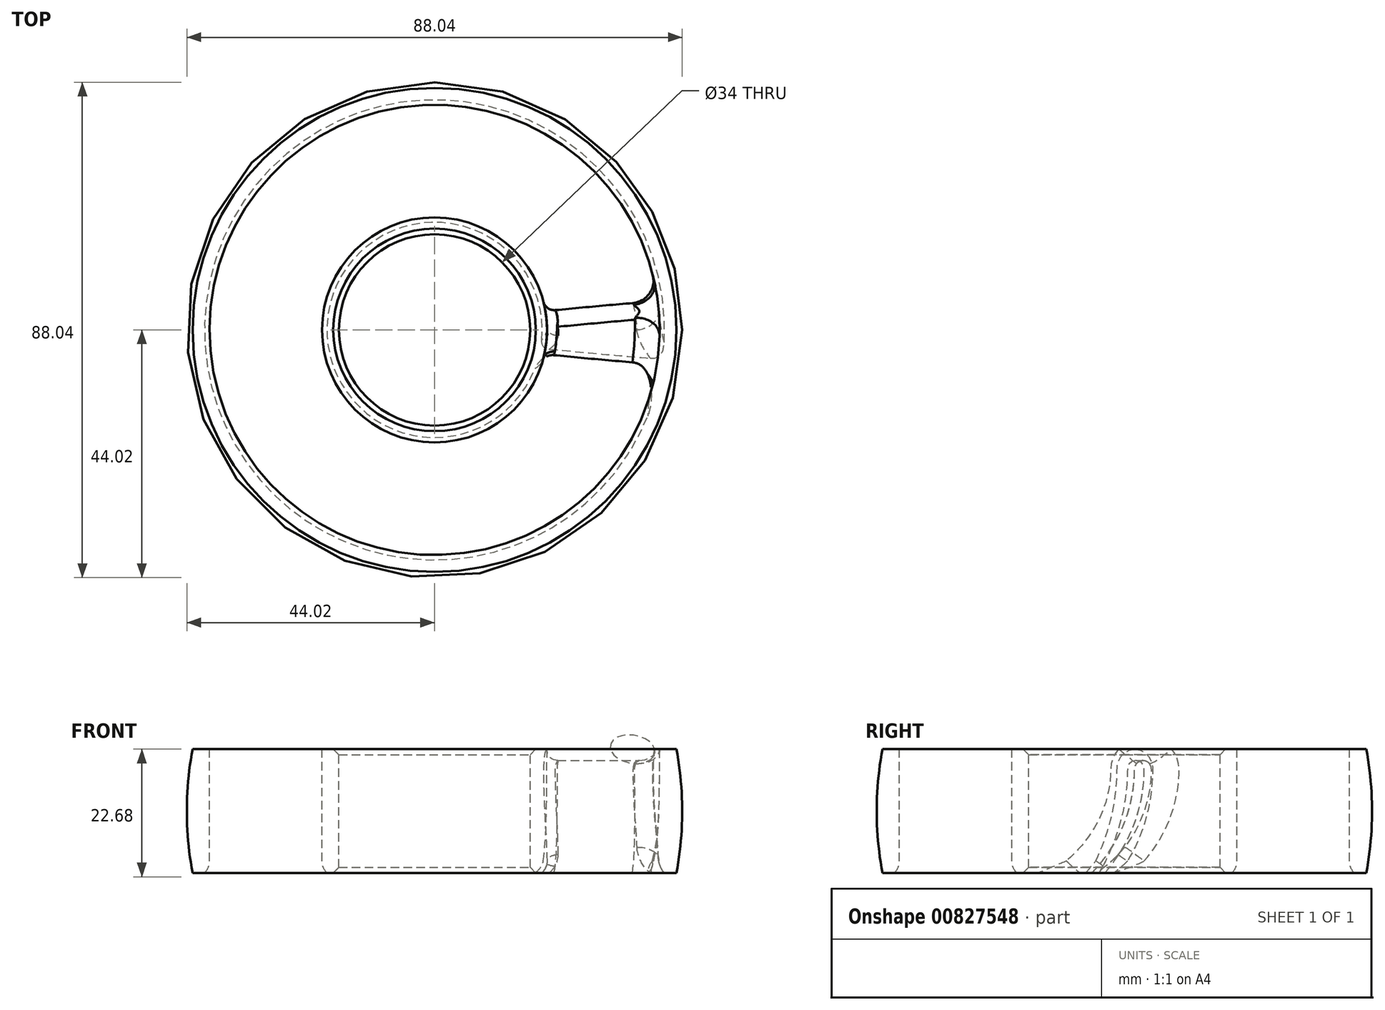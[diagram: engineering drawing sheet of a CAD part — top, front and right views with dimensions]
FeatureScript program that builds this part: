
annotation { "Feature Type Name" : "Feature", "Feature Type Description" : "" }
export const myFeature = defineFeature(function(context is Context, id is Id, definition is map)
    precondition{}
    {
        {
            var Q0;
            Q0=qCreatedBy(makeId("Right.planeOp"),FACE);
            cPlane(context, id + "F0", {"entities" : qUnion([Q0]), "cplaneType" : CPlaneType.OFFSET, "offset" : 18 * mm, "width" : 150 * mm, "height" : 150 * mm});
        }
        {
            var Q0;
            Q0=qCreatedBy(makeId("Right.planeOp"),FACE);
            cPlane(context, id + "F1", {"entities" : qUnion([Q0]), "cplaneType" : CPlaneType.OFFSET, "offset" : 30 * mm, "width" : 150 * mm, "height" : 150 * mm});
        }
        {
            var Q0;
            Q0=qCreatedBy(makeId("Right.planeOp"),FACE);
            cPlane(context, id + "F2", {"entities" : qUnion([Q0]), "cplaneType" : CPlaneType.OFFSET, "offset" : 42 * mm, "width" : 150 * mm, "height" : 150 * mm});
        }
        {
            var Q0;
            Q0=qCreatedBy(makeId("Right.planeOp"),FACE);
            var sketch = newSketch(context, id + "F3", { "sketchPlane" : qUnion([Q0])});
            skLineSegment(sketch, "E0.bottom", {"start": v(20, 10) * mm, "end": v(-20, 10) * mm});
            skLineSegment(sketch, "E0.top", {"start": v(20, -10) * mm, "end": v(-20, -10) * mm});
            skLineSegment(sketch, "E0.left", {"start": v(20, 10) * mm, "end": v(20, -10) * mm});
            skLineSegment(sketch, "E0.right", {"start": v(-20, 10) * mm, "end": v(-20, -10) * mm});
            skPoint(sketch, "E0.middle", {"position": v(0, 0) * mm});
            skSolve(sketch);
        }
        {
            var Q0;
            Q0=qCreatedBy(id+"F0.planeOp",FACE);
            var sketch = newSketch(context, id + "F4", { "sketchPlane" : qUnion([Q0])});
            skArc(sketch, "E1", {"start": v(3.19, 8.5) * mm, "mid": v(1.69, 10) * mm, "end": v(0.19, 8.5) * mm});
            skArc(sketch, "E2", {"start": v(-3.19, -10) * mm, "mid": v(1.55, -1.28) * mm, "end": v(3.19, 8.5) * mm});
            skArc(sketch, "E3", {"start": v(-4.19, -10) * mm, "mid": v(-0.92, -1) * mm, "end": v(0.19, 8.5) * mm});
            skLineSegment(sketch, "E4", {"start": v(0.19, 8.5) * mm, "end": v(3.19, 8.5) * mm, "construction": true});
            skLineSegment(sketch, "E5", {"start": v(-3.19, -10) * mm, "end": v(-4.19, -10) * mm});
            skLineSegment(sketch, "E6", {"start": v(-26.86, 8.5) * mm, "end": v(-3.19, -10) * mm, "construction": true});
            skLineSegment(sketch, "E7", {"start": v(3.19, 8.5) * mm, "end": v(3.19, -10) * mm, "construction": true});
            skLineSegment(sketch, "E8", {"start": v(-3.19, -10) * mm, "end": v(3.19, -10) * mm, "construction": true});
            skLineSegment(sketch, "E9", {"start": v(0, 0) * mm, "end": v(0, -10) * mm, "construction": true});
            skSolve(sketch);
        }
        {
            var Q0;
            Q0=qCreatedBy(id+"F1.planeOp",FACE);
            var sketch = newSketch(context, id + "F5", { "sketchPlane" : qUnion([Q0])});
            skArc(sketch, "E10", {"start": v(4.31, 8.5) * mm, "mid": v(2.81, 10) * mm, "end": v(1.31, 8.5) * mm});
            skLineSegment(sketch, "E11", {"start": v(1.31, 8.5) * mm, "end": v(4.31, 8.5) * mm, "construction": true});
            skLineSegment(sketch, "E12", {"start": v(-5.31, -10) * mm, "end": v(-4.31, -10) * mm});
            skArc(sketch, "E13", {"start": v(-4.31, -10) * mm, "mid": v(2.05, -1.7) * mm, "end": v(4.31, 8.5) * mm});
            skArc(sketch, "E14", {"start": v(-5.31, -10) * mm, "mid": v(-0.4, -1.33) * mm, "end": v(1.31, 8.5) * mm});
            skLineSegment(sketch, "E15", {"start": v(-19.84, 8.5) * mm, "end": v(-4.31, -10) * mm, "construction": true});
            skLineSegment(sketch, "E16", {"start": v(4.31, 8.5) * mm, "end": v(4.31, -10) * mm, "construction": true});
            skLineSegment(sketch, "E17", {"start": v(-4.31, -10) * mm, "end": v(4.31, -10) * mm, "construction": true});
            skLineSegment(sketch, "E18", {"start": v(0, 0) * mm, "end": v(0, -10) * mm, "construction": true});
            skSolve(sketch);
        }
        {
            var Q0;
            Q0=qCreatedBy(id+"F2.planeOp",FACE);
            var sketch = newSketch(context, id + "F6", { "sketchPlane" : qUnion([Q0])});
            skArc(sketch, "E19", {"start": v(5.34, 8.5) * mm, "mid": v(3.84, 10) * mm, "end": v(2.34, 8.5) * mm});
            skLineSegment(sketch, "E20", {"start": v(-6.34, -10) * mm, "end": v(-5.34, -10) * mm});
            skLineSegment(sketch, "E21", {"start": v(2.34, 8.5) * mm, "end": v(5.34, 8.5) * mm, "construction": true});
            skArc(sketch, "E22", {"start": v(-5.34, -10) * mm, "mid": v(2.48, -2.18) * mm, "end": v(5.34, 8.5) * mm});
            skArc(sketch, "E23", {"start": v(-6.34, -10) * mm, "mid": v(0.06, -1.72) * mm, "end": v(2.34, 8.5) * mm});
            skLineSegment(sketch, "E24", {"start": v(-16.02, 8.5) * mm, "end": v(-5.34, -10) * mm, "construction": true});
            skLineSegment(sketch, "E25", {"start": v(5.34, 8.5) * mm, "end": v(5.34, -10) * mm, "construction": true});
            skLineSegment(sketch, "E26", {"start": v(-5.34, -10) * mm, "end": v(5.34, -10) * mm, "construction": true});
            skLineSegment(sketch, "E27", {"start": v(0, 0) * mm, "end": v(0, -10) * mm, "construction": true});
            skSolve(sketch);
        }
        {
            var Q0;
            Q0=makeQuery(id+"F4.imprint","IMPRINT",FACE,{"disambiguationData":[TD([[makeQuery(id+"F4.imprint","IMPRINT",EDGE,{"derivedFrom":sQuery(id+"F4.wireOp",EDGE,"E1")}),1.0]])]});
            var Q1;
            Q1=makeQuery(id+"F5.imprint","IMPRINT",FACE,{"disambiguationData":[TD([[makeQuery(id+"F5.imprint","IMPRINT",EDGE,{"derivedFrom":sQuery(id+"F5.wireOp",EDGE,"E10")}),1.0]])]});
            var Q2;
            Q2=makeQuery(id+"F6.imprint","IMPRINT",FACE,{"disambiguationData":[TD([[makeQuery(id+"F6.imprint","IMPRINT",EDGE,{"derivedFrom":sQuery(id+"F6.wireOp",EDGE,"E19")}),1.0]])]});
            loft(context, id + "F7", {"sheetProfilesArray" : [{ "sheetProfileEntities" : qUnion([Q0]) }, { "sheetProfileEntities" : qUnion([Q1]) }, { "sheetProfileEntities" : qUnion([Q2]) }]});
        }
        {
            var Q0;
            Q0=qCreatedBy(makeId("Front.planeOp"),FACE);
            var sketch = newSketch(context, id + "F8", { "sketchPlane" : qUnion([Q0])});
            skLineSegment(sketch, "E28", {"start": v(20, 12) * mm, "end": v(17, 12) * mm});
            skLineSegment(sketch, "E29", {"start": v(17, 12) * mm, "end": v(17, -10) * mm});
            skLineSegment(sketch, "E30", {"start": v(17, -10) * mm, "end": v(19.12, -10) * mm});
            skLineSegment(sketch, "E31", {"start": v(40, 12) * mm, "end": v(43, 12) * mm});
            skLineSegment(sketch, "E32", {"start": v(43, 12) * mm, "end": v(43, -10) * mm, "construction": true});
            skLineSegment(sketch, "E33", {"start": v(43, -10) * mm, "end": v(40.88, -10) * mm});
            skArc(sketch, "E34", {"start": v(40, -7.88) * mm, "mid": v(40.23, -9.03) * mm, "end": v(40.88, -10) * mm});
            skArc(sketch, "E35", {"start": v(19.12, -10) * mm, "mid": v(19.77, -9.03) * mm, "end": v(20, -7.88) * mm});
            skLineSegment(sketch, "E36", {"start": v(17, -7.88) * mm, "end": v(19.12, -10) * mm, "construction": true});
            skLineSegment(sketch, "E37", {"start": v(43, -7.88) * mm, "end": v(40.88, -10) * mm, "construction": true});
            skLineSegment(sketch, "E38", {"start": v(0, 12) * mm, "end": v(0, -10) * mm, "construction": true});
            skLineSegment(sketch, "E39", {"start": v(20, 12) * mm, "end": v(20, -7.88) * mm});
            skLineSegment(sketch, "E40", {"start": v(40, -7.88) * mm, "end": v(40, 12) * mm});
            skArc(sketch, "E41", {"start": v(43, -10) * mm, "mid": v(44.02, 1) * mm, "end": v(43, 12) * mm});
            skSolve(sketch);
        }
        {
            var Q0;
            Q0=makeQuery(id+"F8.imprint","IMPRINT",FACE,{"disambiguationData":[TD([[makeQuery(id+"F8.imprint","IMPRINT",EDGE,{"derivedFrom":sQuery(id+"F8.wireOp",EDGE,"E28")}),1.0]])]});
            var Q1;
            Q1=sQuery(id+"F8.wireOp",EDGE,"E38");
            revolve(context, id + "F9", {"operationType" : NewBodyOperationType.ADD, "surfaceOperationType" : NewSurfaceOperationType.NEW, "entities" : qUnion([Q0]), "axis" : qUnion([Q1]), "revolveType" : RevolveType.FULL});
        }
        {
            var Q0;
            Q0=makeQuery(id+"F8.imprint","IMPRINT",FACE,{"disambiguationData":[TD([[makeQuery(id+"F8.imprint","IMPRINT",EDGE,{"derivedFrom":sQuery(id+"F8.wireOp",EDGE,"E31")}),-1.0]])]});
            var Q1;
            Q1=sQuery(id+"F8.wireOp",EDGE,"E38");
            revolve(context, id + "F10", {"operationType" : NewBodyOperationType.ADD, "surfaceOperationType" : NewSurfaceOperationType.NEW, "entities" : qUnion([Q0]), "axis" : qUnion([Q1]), "revolveType" : RevolveType.FULL});
        }
        {
            var Q0;
            Q0=makeQuery(id+"F9.boolean.opBoolean","INTERSECT",EDGE,{"derivedFrom":[makeQuery(id+"F7JlVhXRLtaunjP_1.6.F7.opLoft","SWEPT_FACE",FACE,{"disambiguationData":[OSD([sQuery(id+"F4.wireOp",EDGE,"E1"),sQuery(id+"F4.wireOp",EDGE,"E2"),sQuery(id+"F4.wireOp",EDGE,"E5"),sQuery(id+"F5.wireOp",EDGE,"E10"),sQuery(id+"F5.wireOp",EDGE,"E12"),sQuery(id+"F5.wireOp",EDGE,"E13")])]}),makeQuery(id+"F9.opRevolve","SWEPT_FACE",FACE,{"disambiguationData":[OSD([sQuery(id+"F8.wireOp",EDGE,"E39")])]})]});
            var Q1;
            Q1=makeQuery(id+"F9.boolean.opBoolean","INTERSECT",EDGE,{"derivedFrom":[makeQuery(id+"F7JlVhXRLtaunjP_1.5.F7.opLoft","SWEPT_FACE",FACE,{"disambiguationData":[OSD([sQuery(id+"F4.wireOp",EDGE,"E1"),sQuery(id+"F4.wireOp",EDGE,"E2"),sQuery(id+"F4.wireOp",EDGE,"E5"),sQuery(id+"F5.wireOp",EDGE,"E10"),sQuery(id+"F5.wireOp",EDGE,"E12"),sQuery(id+"F5.wireOp",EDGE,"E13")])]}),makeQuery(id+"F9.opRevolve","SWEPT_FACE",FACE,{"disambiguationData":[OSD([sQuery(id+"F8.wireOp",EDGE,"E39")])]})]});
            var Q2;
            Q2=makeQuery(id+"F9.boolean.opBoolean","INTERSECT",EDGE,{"derivedFrom":[makeQuery(id+"F7JlVhXRLtaunjP_1.4.F7.opLoft","SWEPT_FACE",FACE,{"disambiguationData":[OSD([sQuery(id+"F4.wireOp",EDGE,"E1"),sQuery(id+"F4.wireOp",EDGE,"E2"),sQuery(id+"F4.wireOp",EDGE,"E5"),sQuery(id+"F5.wireOp",EDGE,"E10"),sQuery(id+"F5.wireOp",EDGE,"E12"),sQuery(id+"F5.wireOp",EDGE,"E13")])]}),makeQuery(id+"F9.opRevolve","SWEPT_FACE",FACE,{"disambiguationData":[OSD([sQuery(id+"F8.wireOp",EDGE,"E39")])]})]});
            var Q3;
            Q3=makeQuery(id+"F9.boolean.opBoolean","INTERSECT",EDGE,{"derivedFrom":[makeQuery(id+"F7JlVhXRLtaunjP_1.3.F7.opLoft","SWEPT_FACE",FACE,{"disambiguationData":[OSD([sQuery(id+"F4.wireOp",EDGE,"E1"),sQuery(id+"F4.wireOp",EDGE,"E2"),sQuery(id+"F4.wireOp",EDGE,"E5"),sQuery(id+"F5.wireOp",EDGE,"E10"),sQuery(id+"F5.wireOp",EDGE,"E12"),sQuery(id+"F5.wireOp",EDGE,"E13")])]}),makeQuery(id+"F9.opRevolve","SWEPT_FACE",FACE,{"disambiguationData":[OSD([sQuery(id+"F8.wireOp",EDGE,"E39")])]})]});
            var Q4;
            Q4=makeQuery(id+"F9.boolean.opBoolean","INTERSECT",EDGE,{"derivedFrom":[makeQuery(id+"F7JlVhXRLtaunjP_1.2.F7.opLoft","SWEPT_FACE",FACE,{"disambiguationData":[OSD([sQuery(id+"F4.wireOp",EDGE,"E1"),sQuery(id+"F4.wireOp",EDGE,"E2"),sQuery(id+"F4.wireOp",EDGE,"E5"),sQuery(id+"F5.wireOp",EDGE,"E10"),sQuery(id+"F5.wireOp",EDGE,"E12"),sQuery(id+"F5.wireOp",EDGE,"E13")])]}),makeQuery(id+"F9.opRevolve","SWEPT_FACE",FACE,{"disambiguationData":[OSD([sQuery(id+"F8.wireOp",EDGE,"E39")])]})]});
            var Q5;
            Q5=makeQuery(id+"F9.boolean.opBoolean","INTERSECT",EDGE,{"derivedFrom":[makeQuery(id+"F7JlVhXRLtaunjP_1.1.F7.opLoft","SWEPT_FACE",FACE,{"disambiguationData":[OSD([sQuery(id+"F4.wireOp",EDGE,"E1"),sQuery(id+"F4.wireOp",EDGE,"E2"),sQuery(id+"F4.wireOp",EDGE,"E5"),sQuery(id+"F5.wireOp",EDGE,"E10"),sQuery(id+"F5.wireOp",EDGE,"E12"),sQuery(id+"F5.wireOp",EDGE,"E13")])]}),makeQuery(id+"F9.opRevolve","SWEPT_FACE",FACE,{"disambiguationData":[OSD([sQuery(id+"F8.wireOp",EDGE,"E39")])]})]});
            var Q6;
            Q6=makeQuery(id+"F9.boolean.opBoolean","INTERSECT",EDGE,{"derivedFrom":[makeQuery(id+"F7.opLoft","SWEPT_FACE",FACE,{"disambiguationData":[OSD([sQuery(id+"F4.wireOp",EDGE,"E1"),sQuery(id+"F4.wireOp",EDGE,"E2"),sQuery(id+"F4.wireOp",EDGE,"E5"),sQuery(id+"F5.wireOp",EDGE,"E10"),sQuery(id+"F5.wireOp",EDGE,"E12"),sQuery(id+"F5.wireOp",EDGE,"E13")])]}),makeQuery(id+"F9.opRevolve","SWEPT_FACE",FACE,{"disambiguationData":[OSD([sQuery(id+"F8.wireOp",EDGE,"E39")])]})]});
            var Q7;
            Q7=makeQuery(id+"F9.boolean.opBoolean","INTERSECT",EDGE,{"derivedFrom":[makeQuery(id+"F7JlVhXRLtaunjP_1.16.F7.opLoft","SWEPT_FACE",FACE,{"disambiguationData":[OSD([sQuery(id+"F4.wireOp",EDGE,"E1"),sQuery(id+"F4.wireOp",EDGE,"E2"),sQuery(id+"F4.wireOp",EDGE,"E5"),sQuery(id+"F5.wireOp",EDGE,"E10"),sQuery(id+"F5.wireOp",EDGE,"E12"),sQuery(id+"F5.wireOp",EDGE,"E13")])]}),makeQuery(id+"F9.opRevolve","SWEPT_FACE",FACE,{"disambiguationData":[OSD([sQuery(id+"F8.wireOp",EDGE,"E39")])]})]});
            var Q8;
            Q8=makeQuery(id+"F9.boolean.opBoolean","INTERSECT",EDGE,{"derivedFrom":[makeQuery(id+"F7JlVhXRLtaunjP_1.15.F7.opLoft","SWEPT_FACE",FACE,{"disambiguationData":[OSD([sQuery(id+"F4.wireOp",EDGE,"E1"),sQuery(id+"F4.wireOp",EDGE,"E2"),sQuery(id+"F4.wireOp",EDGE,"E5"),sQuery(id+"F5.wireOp",EDGE,"E10"),sQuery(id+"F5.wireOp",EDGE,"E12"),sQuery(id+"F5.wireOp",EDGE,"E13")])]}),makeQuery(id+"F9.opRevolve","SWEPT_FACE",FACE,{"disambiguationData":[OSD([sQuery(id+"F8.wireOp",EDGE,"E39")])]})]});
            var Q9;
            Q9=makeQuery(id+"F9.boolean.opBoolean","INTERSECT",EDGE,{"derivedFrom":[makeQuery(id+"F7JlVhXRLtaunjP_1.14.F7.opLoft","SWEPT_FACE",FACE,{"disambiguationData":[OSD([sQuery(id+"F4.wireOp",EDGE,"E1"),sQuery(id+"F4.wireOp",EDGE,"E2"),sQuery(id+"F4.wireOp",EDGE,"E5"),sQuery(id+"F5.wireOp",EDGE,"E10"),sQuery(id+"F5.wireOp",EDGE,"E12"),sQuery(id+"F5.wireOp",EDGE,"E13")])]}),makeQuery(id+"F9.opRevolve","SWEPT_FACE",FACE,{"disambiguationData":[OSD([sQuery(id+"F8.wireOp",EDGE,"E39")])]})]});
            var Q10;
            Q10=makeQuery(id+"F9.boolean.opBoolean","INTERSECT",EDGE,{"derivedFrom":[makeQuery(id+"F7JlVhXRLtaunjP_1.13.F7.opLoft","SWEPT_FACE",FACE,{"disambiguationData":[OSD([sQuery(id+"F4.wireOp",EDGE,"E1"),sQuery(id+"F4.wireOp",EDGE,"E2"),sQuery(id+"F4.wireOp",EDGE,"E5"),sQuery(id+"F5.wireOp",EDGE,"E10"),sQuery(id+"F5.wireOp",EDGE,"E12"),sQuery(id+"F5.wireOp",EDGE,"E13")])]}),makeQuery(id+"F9.opRevolve","SWEPT_FACE",FACE,{"disambiguationData":[OSD([sQuery(id+"F8.wireOp",EDGE,"E39")])]})]});
            var Q11;
            Q11=makeQuery(id+"F9.boolean.opBoolean","INTERSECT",EDGE,{"derivedFrom":[makeQuery(id+"F7JlVhXRLtaunjP_1.12.F7.opLoft","SWEPT_FACE",FACE,{"disambiguationData":[OSD([sQuery(id+"F4.wireOp",EDGE,"E1"),sQuery(id+"F4.wireOp",EDGE,"E2"),sQuery(id+"F4.wireOp",EDGE,"E5"),sQuery(id+"F5.wireOp",EDGE,"E10"),sQuery(id+"F5.wireOp",EDGE,"E12"),sQuery(id+"F5.wireOp",EDGE,"E13")])]}),makeQuery(id+"F9.opRevolve","SWEPT_FACE",FACE,{"disambiguationData":[OSD([sQuery(id+"F8.wireOp",EDGE,"E39")])]})]});
            var Q12;
            Q12=makeQuery(id+"F9.boolean.opBoolean","INTERSECT",EDGE,{"derivedFrom":[makeQuery(id+"F7JlVhXRLtaunjP_1.11.F7.opLoft","SWEPT_FACE",FACE,{"disambiguationData":[OSD([sQuery(id+"F4.wireOp",EDGE,"E1"),sQuery(id+"F4.wireOp",EDGE,"E2"),sQuery(id+"F4.wireOp",EDGE,"E5"),sQuery(id+"F5.wireOp",EDGE,"E10"),sQuery(id+"F5.wireOp",EDGE,"E12"),sQuery(id+"F5.wireOp",EDGE,"E13")])]}),makeQuery(id+"F9.opRevolve","SWEPT_FACE",FACE,{"disambiguationData":[OSD([sQuery(id+"F8.wireOp",EDGE,"E39")])]})]});
            var Q13;
            Q13=makeQuery(id+"F9.boolean.opBoolean","INTERSECT",EDGE,{"derivedFrom":[makeQuery(id+"F7JlVhXRLtaunjP_1.10.F7.opLoft","SWEPT_FACE",FACE,{"disambiguationData":[OSD([sQuery(id+"F4.wireOp",EDGE,"E1"),sQuery(id+"F4.wireOp",EDGE,"E2"),sQuery(id+"F4.wireOp",EDGE,"E5"),sQuery(id+"F5.wireOp",EDGE,"E10"),sQuery(id+"F5.wireOp",EDGE,"E12"),sQuery(id+"F5.wireOp",EDGE,"E13")])]}),makeQuery(id+"F9.opRevolve","SWEPT_FACE",FACE,{"disambiguationData":[OSD([sQuery(id+"F8.wireOp",EDGE,"E39")])]})]});
            var Q14;
            Q14=makeQuery(id+"F9.boolean.opBoolean","INTERSECT",EDGE,{"derivedFrom":[makeQuery(id+"F7JlVhXRLtaunjP_1.9.F7.opLoft","SWEPT_FACE",FACE,{"disambiguationData":[OSD([sQuery(id+"F4.wireOp",EDGE,"E1"),sQuery(id+"F4.wireOp",EDGE,"E2"),sQuery(id+"F4.wireOp",EDGE,"E5"),sQuery(id+"F5.wireOp",EDGE,"E10"),sQuery(id+"F5.wireOp",EDGE,"E12"),sQuery(id+"F5.wireOp",EDGE,"E13")])]}),makeQuery(id+"F9.opRevolve","SWEPT_FACE",FACE,{"disambiguationData":[OSD([sQuery(id+"F8.wireOp",EDGE,"E39")])]})]});
            var Q15;
            Q15=makeQuery(id+"F9.boolean.opBoolean","INTERSECT",EDGE,{"derivedFrom":[makeQuery(id+"F7JlVhXRLtaunjP_1.8.F7.opLoft","SWEPT_FACE",FACE,{"disambiguationData":[OSD([sQuery(id+"F4.wireOp",EDGE,"E1"),sQuery(id+"F4.wireOp",EDGE,"E2"),sQuery(id+"F4.wireOp",EDGE,"E5"),sQuery(id+"F5.wireOp",EDGE,"E10"),sQuery(id+"F5.wireOp",EDGE,"E12"),sQuery(id+"F5.wireOp",EDGE,"E13")])]}),makeQuery(id+"F9.opRevolve","SWEPT_FACE",FACE,{"disambiguationData":[OSD([sQuery(id+"F8.wireOp",EDGE,"E39")])]})]});
            var Q16;
            Q16=makeQuery(id+"F9.boolean.opBoolean","INTERSECT",EDGE,{"derivedFrom":[makeQuery(id+"F7JlVhXRLtaunjP_1.7.F7.opLoft","SWEPT_FACE",FACE,{"disambiguationData":[OSD([sQuery(id+"F4.wireOp",EDGE,"E1"),sQuery(id+"F4.wireOp",EDGE,"E2"),sQuery(id+"F4.wireOp",EDGE,"E5"),sQuery(id+"F5.wireOp",EDGE,"E10"),sQuery(id+"F5.wireOp",EDGE,"E12"),sQuery(id+"F5.wireOp",EDGE,"E13")])]}),makeQuery(id+"F9.opRevolve","SWEPT_FACE",FACE,{"disambiguationData":[OSD([sQuery(id+"F8.wireOp",EDGE,"E39")])]})]});
            fillet(context, id + "F11", {"entities" : qUnion([Q0, Q1, Q2, Q3, Q4, Q5, Q6, Q7, Q8, Q9, Q10, Q11, Q12, Q13, Q14, Q15, Q16]), "radius" : 2 * mm, "tangentPropagation" : true, "allowEdgeOverflow" : false});
        }
        {
            var Q0;
            Q0=makeQuery(id+"F10.boolean.opBoolean","INTERSECT",EDGE,{"derivedFrom":[makeQuery(id+"F7.opLoft","SWEPT_FACE",FACE,{"disambiguationData":[OSD([sQuery(id+"F4.wireOp",EDGE,"E1"),sQuery(id+"F4.wireOp",EDGE,"E2"),sQuery(id+"F4.wireOp",EDGE,"E5"),sQuery(id+"F5.wireOp",EDGE,"E10"),sQuery(id+"F5.wireOp",EDGE,"E12"),sQuery(id+"F5.wireOp",EDGE,"E13")])]}),makeQuery(id+"F10.opRevolve","SWEPT_FACE",FACE,{"disambiguationData":[OSD([sQuery(id+"F8.wireOp",EDGE,"E40")])]})]});
            var Q1;
            Q1=makeQuery(id+"F10.boolean.opBoolean","INTERSECT",EDGE,{"derivedFrom":[makeQuery(id+"F7JlVhXRLtaunjP_1.1.F7.opLoft","SWEPT_FACE",FACE,{"disambiguationData":[OSD([sQuery(id+"F4.wireOp",EDGE,"E1"),sQuery(id+"F4.wireOp",EDGE,"E2"),sQuery(id+"F4.wireOp",EDGE,"E5"),sQuery(id+"F5.wireOp",EDGE,"E10"),sQuery(id+"F5.wireOp",EDGE,"E12"),sQuery(id+"F5.wireOp",EDGE,"E13")])]}),makeQuery(id+"F10.opRevolve","SWEPT_FACE",FACE,{"disambiguationData":[OSD([sQuery(id+"F8.wireOp",EDGE,"E40")])]})]});
            var Q2;
            Q2=makeQuery(id+"F10.boolean.opBoolean","INTERSECT",EDGE,{"derivedFrom":[makeQuery(id+"F7JlVhXRLtaunjP_1.2.F7.opLoft","SWEPT_FACE",FACE,{"disambiguationData":[OSD([sQuery(id+"F4.wireOp",EDGE,"E1"),sQuery(id+"F4.wireOp",EDGE,"E2"),sQuery(id+"F4.wireOp",EDGE,"E5"),sQuery(id+"F5.wireOp",EDGE,"E10"),sQuery(id+"F5.wireOp",EDGE,"E12"),sQuery(id+"F5.wireOp",EDGE,"E13")])]}),makeQuery(id+"F10.opRevolve","SWEPT_FACE",FACE,{"disambiguationData":[OSD([sQuery(id+"F8.wireOp",EDGE,"E40")])]})]});
            var Q3;
            Q3=makeQuery(id+"F10.boolean.opBoolean","INTERSECT",EDGE,{"derivedFrom":[makeQuery(id+"F7JlVhXRLtaunjP_1.3.F7.opLoft","SWEPT_FACE",FACE,{"disambiguationData":[OSD([sQuery(id+"F4.wireOp",EDGE,"E1"),sQuery(id+"F4.wireOp",EDGE,"E2"),sQuery(id+"F4.wireOp",EDGE,"E5"),sQuery(id+"F5.wireOp",EDGE,"E10"),sQuery(id+"F5.wireOp",EDGE,"E12"),sQuery(id+"F5.wireOp",EDGE,"E13")])]}),makeQuery(id+"F10.opRevolve","SWEPT_FACE",FACE,{"disambiguationData":[OSD([sQuery(id+"F8.wireOp",EDGE,"E40")])]})]});
            var Q4;
            Q4=makeQuery(id+"F10.boolean.opBoolean","INTERSECT",EDGE,{"derivedFrom":[makeQuery(id+"F7JlVhXRLtaunjP_1.4.F7.opLoft","SWEPT_FACE",FACE,{"disambiguationData":[OSD([sQuery(id+"F4.wireOp",EDGE,"E1"),sQuery(id+"F4.wireOp",EDGE,"E2"),sQuery(id+"F4.wireOp",EDGE,"E5"),sQuery(id+"F5.wireOp",EDGE,"E10"),sQuery(id+"F5.wireOp",EDGE,"E12"),sQuery(id+"F5.wireOp",EDGE,"E13")])]}),makeQuery(id+"F10.opRevolve","SWEPT_FACE",FACE,{"disambiguationData":[OSD([sQuery(id+"F8.wireOp",EDGE,"E40")])]})]});
            var Q5;
            Q5=makeQuery(id+"F10.boolean.opBoolean","INTERSECT",EDGE,{"derivedFrom":[makeQuery(id+"F7JlVhXRLtaunjP_1.5.F7.opLoft","SWEPT_FACE",FACE,{"disambiguationData":[OSD([sQuery(id+"F4.wireOp",EDGE,"E1"),sQuery(id+"F4.wireOp",EDGE,"E2"),sQuery(id+"F4.wireOp",EDGE,"E5"),sQuery(id+"F5.wireOp",EDGE,"E10"),sQuery(id+"F5.wireOp",EDGE,"E12"),sQuery(id+"F5.wireOp",EDGE,"E13")])]}),makeQuery(id+"F10.opRevolve","SWEPT_FACE",FACE,{"disambiguationData":[OSD([sQuery(id+"F8.wireOp",EDGE,"E40")])]})]});
            var Q6;
            Q6=makeQuery(id+"F10.boolean.opBoolean","INTERSECT",EDGE,{"derivedFrom":[makeQuery(id+"F7JlVhXRLtaunjP_1.6.F7.opLoft","SWEPT_FACE",FACE,{"disambiguationData":[OSD([sQuery(id+"F4.wireOp",EDGE,"E1"),sQuery(id+"F4.wireOp",EDGE,"E2"),sQuery(id+"F4.wireOp",EDGE,"E5"),sQuery(id+"F5.wireOp",EDGE,"E10"),sQuery(id+"F5.wireOp",EDGE,"E12"),sQuery(id+"F5.wireOp",EDGE,"E13")])]}),makeQuery(id+"F10.opRevolve","SWEPT_FACE",FACE,{"disambiguationData":[OSD([sQuery(id+"F8.wireOp",EDGE,"E40")])]})]});
            var Q7;
            Q7=makeQuery(id+"F10.boolean.opBoolean","INTERSECT",EDGE,{"derivedFrom":[makeQuery(id+"F7JlVhXRLtaunjP_1.7.F7.opLoft","SWEPT_FACE",FACE,{"disambiguationData":[OSD([sQuery(id+"F4.wireOp",EDGE,"E1"),sQuery(id+"F4.wireOp",EDGE,"E2"),sQuery(id+"F4.wireOp",EDGE,"E5"),sQuery(id+"F5.wireOp",EDGE,"E10"),sQuery(id+"F5.wireOp",EDGE,"E12"),sQuery(id+"F5.wireOp",EDGE,"E13")])]}),makeQuery(id+"F10.opRevolve","SWEPT_FACE",FACE,{"disambiguationData":[OSD([sQuery(id+"F8.wireOp",EDGE,"E40")])]})]});
            var Q8;
            Q8=makeQuery(id+"F10.boolean.opBoolean","INTERSECT",EDGE,{"derivedFrom":[makeQuery(id+"F7JlVhXRLtaunjP_1.8.F7.opLoft","SWEPT_FACE",FACE,{"disambiguationData":[OSD([sQuery(id+"F4.wireOp",EDGE,"E1"),sQuery(id+"F4.wireOp",EDGE,"E2"),sQuery(id+"F4.wireOp",EDGE,"E5"),sQuery(id+"F5.wireOp",EDGE,"E10"),sQuery(id+"F5.wireOp",EDGE,"E12"),sQuery(id+"F5.wireOp",EDGE,"E13")])]}),makeQuery(id+"F10.opRevolve","SWEPT_FACE",FACE,{"disambiguationData":[OSD([sQuery(id+"F8.wireOp",EDGE,"E40")])]})]});
            var Q9;
            Q9=makeQuery(id+"F10.boolean.opBoolean","INTERSECT",EDGE,{"derivedFrom":[makeQuery(id+"F7JlVhXRLtaunjP_1.9.F7.opLoft","SWEPT_FACE",FACE,{"disambiguationData":[OSD([sQuery(id+"F4.wireOp",EDGE,"E1"),sQuery(id+"F4.wireOp",EDGE,"E2"),sQuery(id+"F4.wireOp",EDGE,"E5"),sQuery(id+"F5.wireOp",EDGE,"E10"),sQuery(id+"F5.wireOp",EDGE,"E12"),sQuery(id+"F5.wireOp",EDGE,"E13")])]}),makeQuery(id+"F10.opRevolve","SWEPT_FACE",FACE,{"disambiguationData":[OSD([sQuery(id+"F8.wireOp",EDGE,"E40")])]})]});
            var Q10;
            Q10=makeQuery(id+"F10.boolean.opBoolean","INTERSECT",EDGE,{"derivedFrom":[makeQuery(id+"F7JlVhXRLtaunjP_1.10.F7.opLoft","SWEPT_FACE",FACE,{"disambiguationData":[OSD([sQuery(id+"F4.wireOp",EDGE,"E1"),sQuery(id+"F4.wireOp",EDGE,"E2"),sQuery(id+"F4.wireOp",EDGE,"E5"),sQuery(id+"F5.wireOp",EDGE,"E10"),sQuery(id+"F5.wireOp",EDGE,"E12"),sQuery(id+"F5.wireOp",EDGE,"E13")])]}),makeQuery(id+"F10.opRevolve","SWEPT_FACE",FACE,{"disambiguationData":[OSD([sQuery(id+"F8.wireOp",EDGE,"E40")])]})]});
            var Q11;
            Q11=makeQuery(id+"F10.boolean.opBoolean","INTERSECT",EDGE,{"derivedFrom":[makeQuery(id+"F7JlVhXRLtaunjP_1.11.F7.opLoft","SWEPT_FACE",FACE,{"disambiguationData":[OSD([sQuery(id+"F4.wireOp",EDGE,"E1"),sQuery(id+"F4.wireOp",EDGE,"E2"),sQuery(id+"F4.wireOp",EDGE,"E5"),sQuery(id+"F5.wireOp",EDGE,"E10"),sQuery(id+"F5.wireOp",EDGE,"E12"),sQuery(id+"F5.wireOp",EDGE,"E13")])]}),makeQuery(id+"F10.opRevolve","SWEPT_FACE",FACE,{"disambiguationData":[OSD([sQuery(id+"F8.wireOp",EDGE,"E40")])]})]});
            var Q12;
            Q12=makeQuery(id+"F10.boolean.opBoolean","INTERSECT",EDGE,{"derivedFrom":[makeQuery(id+"F7JlVhXRLtaunjP_1.12.F7.opLoft","SWEPT_FACE",FACE,{"disambiguationData":[OSD([sQuery(id+"F4.wireOp",EDGE,"E1"),sQuery(id+"F4.wireOp",EDGE,"E2"),sQuery(id+"F4.wireOp",EDGE,"E5"),sQuery(id+"F5.wireOp",EDGE,"E10"),sQuery(id+"F5.wireOp",EDGE,"E12"),sQuery(id+"F5.wireOp",EDGE,"E13")])]}),makeQuery(id+"F10.opRevolve","SWEPT_FACE",FACE,{"disambiguationData":[OSD([sQuery(id+"F8.wireOp",EDGE,"E40")])]})]});
            var Q13;
            Q13=makeQuery(id+"F10.boolean.opBoolean","INTERSECT",EDGE,{"derivedFrom":[makeQuery(id+"F7JlVhXRLtaunjP_1.13.F7.opLoft","SWEPT_FACE",FACE,{"disambiguationData":[OSD([sQuery(id+"F4.wireOp",EDGE,"E1"),sQuery(id+"F4.wireOp",EDGE,"E2"),sQuery(id+"F4.wireOp",EDGE,"E5"),sQuery(id+"F5.wireOp",EDGE,"E10"),sQuery(id+"F5.wireOp",EDGE,"E12"),sQuery(id+"F5.wireOp",EDGE,"E13")])]}),makeQuery(id+"F10.opRevolve","SWEPT_FACE",FACE,{"disambiguationData":[OSD([sQuery(id+"F8.wireOp",EDGE,"E40")])]})]});
            var Q14;
            Q14=makeQuery(id+"F10.boolean.opBoolean","INTERSECT",EDGE,{"derivedFrom":[makeQuery(id+"F7JlVhXRLtaunjP_1.14.F7.opLoft","SWEPT_FACE",FACE,{"disambiguationData":[OSD([sQuery(id+"F4.wireOp",EDGE,"E1"),sQuery(id+"F4.wireOp",EDGE,"E2"),sQuery(id+"F4.wireOp",EDGE,"E5"),sQuery(id+"F5.wireOp",EDGE,"E10"),sQuery(id+"F5.wireOp",EDGE,"E12"),sQuery(id+"F5.wireOp",EDGE,"E13")])]}),makeQuery(id+"F10.opRevolve","SWEPT_FACE",FACE,{"disambiguationData":[OSD([sQuery(id+"F8.wireOp",EDGE,"E40")])]})]});
            var Q15;
            Q15=makeQuery(id+"F10.boolean.opBoolean","INTERSECT",EDGE,{"derivedFrom":[makeQuery(id+"F7JlVhXRLtaunjP_1.15.F7.opLoft","SWEPT_FACE",FACE,{"disambiguationData":[OSD([sQuery(id+"F4.wireOp",EDGE,"E1"),sQuery(id+"F4.wireOp",EDGE,"E2"),sQuery(id+"F4.wireOp",EDGE,"E5"),sQuery(id+"F5.wireOp",EDGE,"E10"),sQuery(id+"F5.wireOp",EDGE,"E12"),sQuery(id+"F5.wireOp",EDGE,"E13")])]}),makeQuery(id+"F10.opRevolve","SWEPT_FACE",FACE,{"disambiguationData":[OSD([sQuery(id+"F8.wireOp",EDGE,"E40")])]})]});
            var Q16;
            Q16=makeQuery(id+"F10.boolean.opBoolean","INTERSECT",EDGE,{"derivedFrom":[makeQuery(id+"F7JlVhXRLtaunjP_1.16.F7.opLoft","SWEPT_FACE",FACE,{"disambiguationData":[OSD([sQuery(id+"F4.wireOp",EDGE,"E1"),sQuery(id+"F4.wireOp",EDGE,"E2"),sQuery(id+"F4.wireOp",EDGE,"E5"),sQuery(id+"F5.wireOp",EDGE,"E10"),sQuery(id+"F5.wireOp",EDGE,"E12"),sQuery(id+"F5.wireOp",EDGE,"E13")])]}),makeQuery(id+"F10.opRevolve","SWEPT_FACE",FACE,{"disambiguationData":[OSD([sQuery(id+"F8.wireOp",EDGE,"E40")])]})]});
            fillet(context, id + "F12", {"entities" : qUnion([Q0, Q1, Q2, Q3, Q4, Q5, Q6, Q7, Q8, Q9, Q10, Q11, Q12, Q13, Q14, Q15, Q16]), "radius" : 4 * mm, "tangentPropagation" : true, "allowEdgeOverflow" : false});
        }
        {
            var Q0;
            Q0=makeQuery(id+"F9.opRevolve","SWEPT_FACE",FACE,{"disambiguationData":[OSD([sQuery(id+"F8.wireOp",EDGE,"E29")])]});
            chamfer(context, id + "F13", {"entities" : qUnion([Q0]), "width" : 1 * mm, "tangentPropagation" : true});
        }
    });
